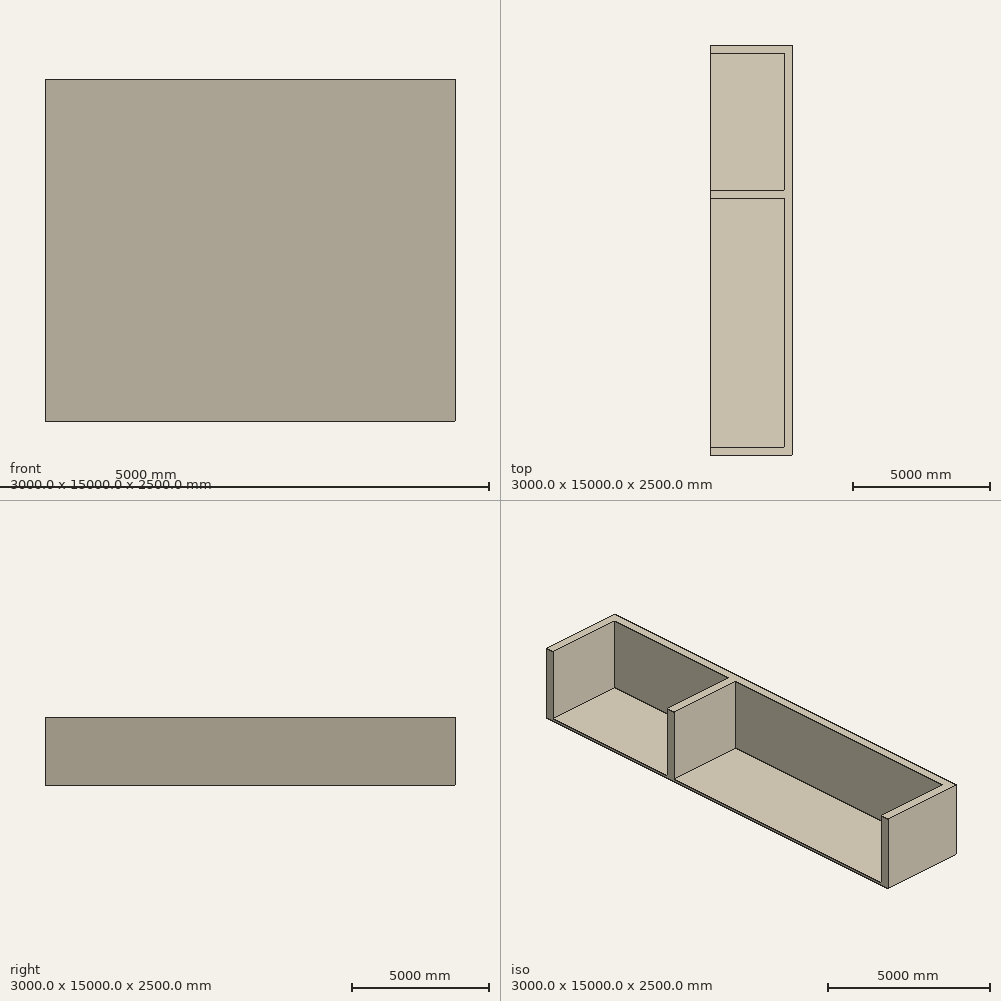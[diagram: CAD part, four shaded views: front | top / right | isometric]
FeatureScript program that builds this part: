
annotation { "Feature Type Name" : "Feature", "Feature Type Description" : "" }
export const myFeature = defineFeature(function(context is Context, id is Id, definition is map)
    precondition{}
    {
        {
            var Q0;
            Q0=qCreatedBy(makeId("Top.planeOp"),FACE);
            var sketch = newSketch(context, id + "F0", { "sketchPlane" : qUnion([Q0])});
            skLineSegment(sketch, "E0.bottom", {"start": v(0, 15000) * mm, "end": v(3000, 15000) * mm});
            skLineSegment(sketch, "E0.top", {"start": v(0, 0) * mm, "end": v(3000, 0) * mm});
            skLineSegment(sketch, "E0.left", {"start": v(0, 15000) * mm, "end": v(0, 0) * mm});
            skLineSegment(sketch, "E0.right", {"start": v(3000, 15000) * mm, "end": v(3000, 0) * mm});
            skSolve(sketch);
        }
        {
            var Q0;
            Q0 = qSketchRegion(id + "F0", true);
            extrude(context, id + "F1", {"entities" : qUnion([Q0]), "depth" : 100 * mm, "offsetDistance" : 25 * mm});
        }
        {
            var Q0;
            Q0=makeQuery(id+"F1.opExtrude","CAP_FACE",FACE,{"disambiguationData":[OSD([sQuery(id+"F0.wireOp",EDGE,"E0.bottom"),sQuery(id+"F0.wireOp",EDGE,"E0.top"),sQuery(id+"F0.wireOp",EDGE,"E0.left"),sQuery(id+"F0.wireOp",EDGE,"E0.right")])],"isStart":false});
            var sketch = newSketch(context, id + "F2", { "sketchPlane" : qUnion([Q0])});
            skLineSegment(sketch, "E1.1", {"start": v(2700, 14700) * mm, "end": v(0, 14700) * mm});
            skLineSegment(sketch, "E1.2", {"start": v(2700, 300) * mm, "end": v(2700, 14700) * mm});
            skLineSegment(sketch, "E1.3", {"start": v(0, 300) * mm, "end": v(2700, 300) * mm});
            skLineSegment(sketch, "E2", {"start": v(0, 15000) * mm, "end": v(3000, 15000) * mm});
            skLineSegment(sketch, "E3", {"start": v(3000, 15000) * mm, "end": v(3000, 0) * mm});
            skLineSegment(sketch, "E4", {"start": v(3000, 0) * mm, "end": v(0, 0) * mm});
            skLineSegment(sketch, "E5", {"start": v(0, 0) * mm, "end": v(0, 300) * mm});
            skLineSegment(sketch, "E6", {"start": v(0, 14700) * mm, "end": v(0, 15000) * mm});
            skLineSegment(sketch, "E7.bottom", {"start": v(2700, 9700) * mm, "end": v(0, 9700) * mm});
            skLineSegment(sketch, "E7.top", {"start": v(2700, 9400) * mm, "end": v(0, 9400) * mm});
            skLineSegment(sketch, "E7.left", {"start": v(2700, 9700) * mm, "end": v(2700, 9400) * mm});
            skLineSegment(sketch, "E7.right", {"start": v(0, 9700) * mm, "end": v(0, 9400) * mm});
            skSolve(sketch);
        }
        {
            var Q0;
            Q0 = qSketchRegion(id + "F2", true);
            extrude(context, id + "F3", {"entities" : qUnion([Q0]), "operationType" : NewBodyOperationType.ADD, "depth" : 2400 * mm, "offsetDistance" : 25 * mm});
        }
    });
